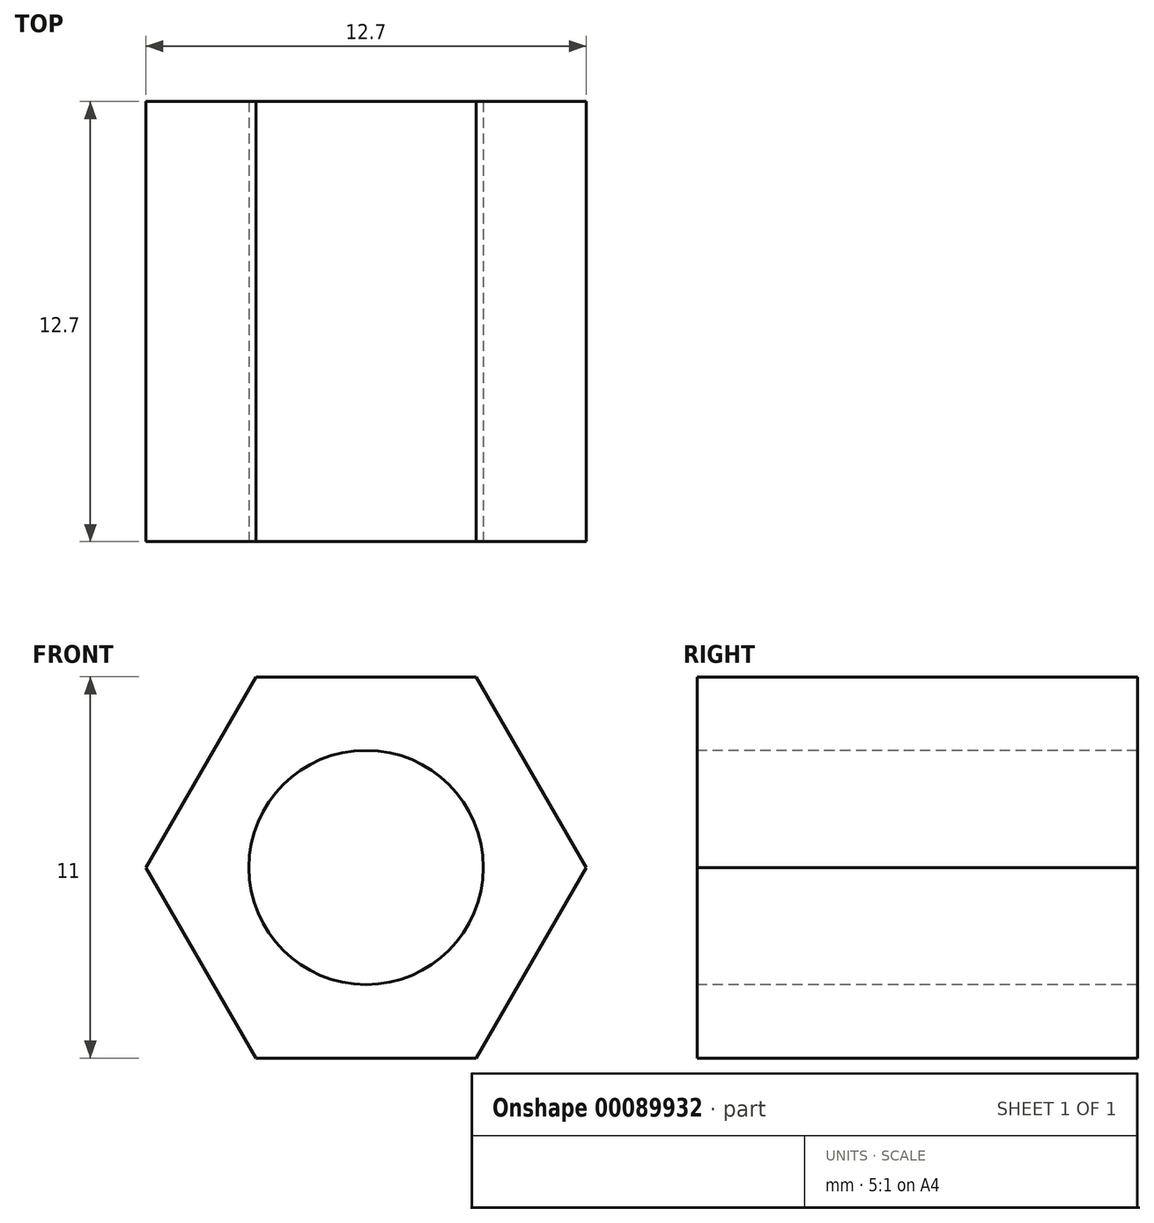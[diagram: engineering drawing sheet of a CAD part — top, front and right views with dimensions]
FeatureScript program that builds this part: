
annotation { "Feature Type Name" : "Feature", "Feature Type Description" : "" }
export const myFeature = defineFeature(function(context is Context, id is Id, definition is map)
    precondition{}
    {
        {
            var Q0;
            Q0=qCreatedBy(makeId("Front.planeOp"),FACE);
            var sketch = newSketch(context, id + "F0", { "sketchPlane" : qUnion([Q0])});
            skLineSegment(sketch, "E0.0", {"start": v(-6.35, 0) * mm, "end": v(-3.18, 5.5) * mm});
            skLineSegment(sketch, "E0.1", {"start": v(-3.18, 5.5) * mm, "end": v(3.17, 5.5) * mm});
            skLineSegment(sketch, "E0.2", {"start": v(3.17, 5.5) * mm, "end": v(6.35, 0) * mm});
            skLineSegment(sketch, "E0.3", {"start": v(6.35, 0) * mm, "end": v(3.18, -5.5) * mm});
            skLineSegment(sketch, "E0.4", {"start": v(3.18, -5.5) * mm, "end": v(-3.17, -5.5) * mm});
            skLineSegment(sketch, "E0.5", {"start": v(-3.17, -5.5) * mm, "end": v(-6.35, 0) * mm});
            skSolve(sketch);
        }
        {
            var Q0;
            Q0=makeQuery(id+"F0.imprint","IMPRINT",FACE,{"disambiguationData":[TD([[makeQuery(id+"F0.imprint","IMPRINT",EDGE,{"derivedFrom":sQuery(id+"F0.wireOp",EDGE,"E0.0")}),-1.0]])]});
            extrude(context, id + "F1", {"entities" : qUnion([Q0]), "depth" : 12.7 * mm});
        }
        {
            var Q0;
            Q0=makeQuery(id+"F1.opExtrude","CAP_FACE",FACE,{"disambiguationData":[OSD([sQuery(id+"F0.wireOp",EDGE,"E0.0"),sQuery(id+"F0.wireOp",EDGE,"E0.1"),sQuery(id+"F0.wireOp",EDGE,"E0.2"),sQuery(id+"F0.wireOp",EDGE,"E0.3"),sQuery(id+"F0.wireOp",EDGE,"E0.4"),sQuery(id+"F0.wireOp",EDGE,"E0.5")])],"isStart":false});
            var sketch = newSketch(context, id + "F2", { "sketchPlane" : qUnion([Q0])});
            skPoint(sketch, "E1", {"position": v(0, 0) * mm});
            skSolve(sketch);
        }
        {
            var Q0;
            Q0=sQuery(id+"F2.wireOp",VERTEX,"E1");
            var Q1;
            Q1=makeQuery(id+"F1.opExtrude","SWEPT_BODY",BODY,{"disambiguationData":[OSD([sQuery(id+"F0.wireOp",EDGE,"E0.0"),sQuery(id+"F0.wireOp",EDGE,"E0.1"),sQuery(id+"F0.wireOp",EDGE,"E0.2"),sQuery(id+"F0.wireOp",EDGE,"E0.3"),sQuery(id+"F0.wireOp",EDGE,"E0.4"),sQuery(id+"F0.wireOp",EDGE,"E0.5")])]});
            hole(context, id + "F3", {"style" : HoleStyle.SIMPLE, "endStyle" : HoleEndStyle.BLIND, "standardTappedOrClearance" : lookupTablePath({ "standard" : "ANSI", "fit" : "Normal (ASME)", "size" : "1/4", "type" : "Clearance" }), "standardBlindInLast" : lookupTablePath({ "fit" : "Free", "standard" : "ANSI", "size" : "1/4", "type" : "Clearance" }), "holeDiameter" : 6.76 * mm, "holeDepth" : 12.7 * mm, "locations" : qUnion([Q0]), "scope" : qUnion([Q1])});
        }
    });
